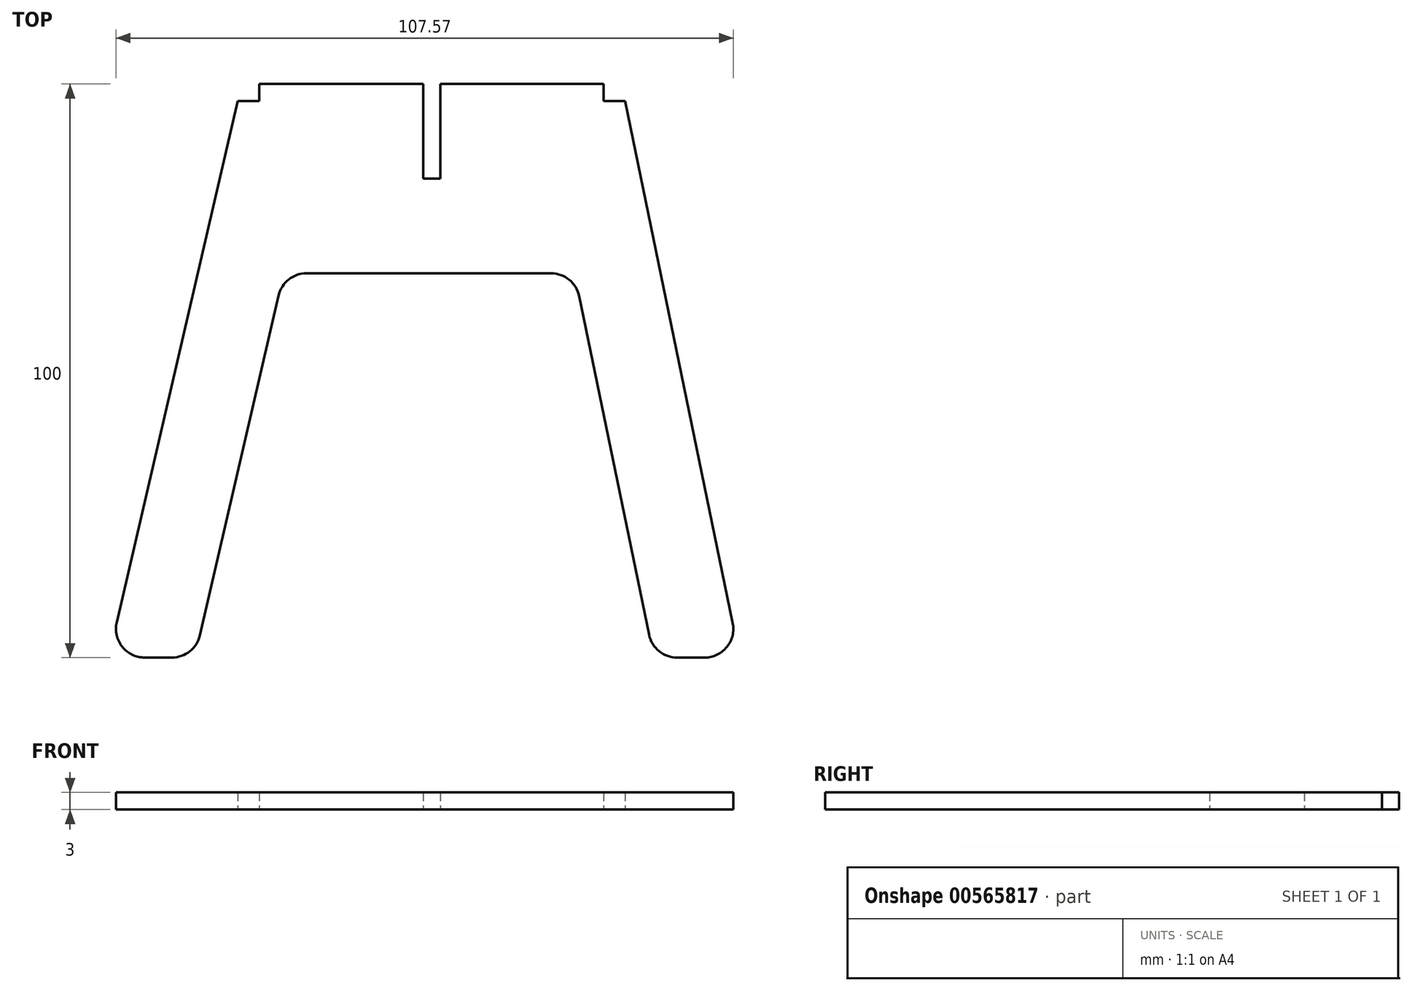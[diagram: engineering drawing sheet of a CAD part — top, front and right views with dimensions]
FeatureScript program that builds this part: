
annotation { "Feature Type Name" : "Feature", "Feature Type Description" : "" }
export const myFeature = defineFeature(function(context is Context, id is Id, definition is map)
    precondition{}
    {
        {
            var Q0;
            Q0=qCreatedBy(makeId("Top.planeOp"),FACE);
            var sketch = newSketch(context, id + "F0", { "sketchPlane" : qUnion([Q0])});
            skLineSegment(sketch, "E0.bottom", {"start": v(-30.08, 50.11) * mm, "end": v(-1.5, 50.11) * mm});
            skLineSegment(sketch, "E0.top", {"start": v(-50.03, -49.89) * mm, "end": v(-45.3, -49.89) * mm});
            skLineSegment(sketch, "E1", {"start": v(-33.84, 47.11) * mm, "end": v(-30.08, 47.11) * mm});
            skLineSegment(sketch, "E2", {"start": v(-30.08, 47.11) * mm, "end": v(-30.08, 50.11) * mm});
            skLineSegment(sketch, "E3", {"start": v(29.92, 47.11) * mm, "end": v(29.92, 50.11) * mm});
            skLineSegment(sketch, "E4", {"start": v(-21.82, 17.11) * mm, "end": v(20.79, 17.11) * mm});
            skLineSegment(sketch, "E5", {"start": v(33.67, 47.11) * mm, "end": v(52.44, -43.88) * mm});
            skLineSegment(sketch, "E6", {"start": v(-54.9, -43.76) * mm, "end": v(-33.84, 47.11) * mm});
            skLineSegment(sketch, "E7", {"start": v(-40.43, -46.02) * mm, "end": v(-26.7, 13.24) * mm});
            skLineSegment(sketch, "E8", {"start": v(25.68, 13.12) * mm, "end": v(37.85, -45.9) * mm});
            skLineSegment(sketch, "E9.trimOffspring", {"start": v(42.75, -49.89) * mm, "end": v(47.54, -49.89) * mm});
            skLineSegment(sketch, "E10.trimOffspring", {"start": v(29.92, 47.11) * mm, "end": v(33.67, 47.11) * mm});
            skPoint(sketch, "E11.visualSharp", {"position": v(-56.33, -49.89) * mm});
            skArc(sketch, "E11.filletArc", {"start": v(-54.9, -43.76) * mm, "mid": v(-53.95, -48) * mm, "end": v(-50.03, -49.89) * mm});
            skPoint(sketch, "E12.visualSharp", {"position": v(-41.33, -49.89) * mm});
            skArc(sketch, "E12.filletArc", {"start": v(-45.3, -49.89) * mm, "mid": v(-42.19, -48.8) * mm, "end": v(-40.43, -46.02) * mm});
            skPoint(sketch, "E13.visualSharp", {"position": v(38.67, -49.89) * mm});
            skArc(sketch, "E13.filletArc", {"start": v(37.85, -45.9) * mm, "mid": v(39.59, -48.77) * mm, "end": v(42.75, -49.89) * mm});
            skPoint(sketch, "E14.visualSharp", {"position": v(53.67, -49.89) * mm});
            skArc(sketch, "E14.filletArc", {"start": v(47.54, -49.89) * mm, "mid": v(51.41, -48.05) * mm, "end": v(52.44, -43.88) * mm});
            skPoint(sketch, "E15.visualSharp", {"position": v(-25.8, 17.11) * mm});
            skArc(sketch, "E15.filletArc", {"start": v(-21.82, 17.11) * mm, "mid": v(-24.93, 16.03) * mm, "end": v(-26.7, 13.24) * mm});
            skPoint(sketch, "E16.visualSharp", {"position": v(24.86, 17.11) * mm});
            skArc(sketch, "E16.filletArc", {"start": v(25.68, 13.12) * mm, "mid": v(23.94, 15.99) * mm, "end": v(20.79, 17.11) * mm});
            skLineSegment(sketch, "E17", {"start": v(0, 50.11) * mm, "end": v(0, 17.11) * mm, "construction": true});
            skLineSegment(sketch, "E18", {"start": v(1.5, 50.11) * mm, "end": v(1.5, 33.61) * mm});
            skPoint(sketch, "E18.endSnap0", {"position": v(0, 33.61) * mm});
            skLineSegment(sketch, "E19.MirrorCS", {"start": v(-1.5, 50.11) * mm, "end": v(-1.5, 33.61) * mm});
            skLineSegment(sketch, "E20", {"start": v(0, 33.61) * mm, "end": v(-1.5, 33.61) * mm});
            skLineSegment(sketch, "E21", {"start": v(0, 33.61) * mm, "end": v(1.5, 33.61) * mm});
            skLineSegment(sketch, "E22.trimOffspring", {"start": v(1.5, 50.11) * mm, "end": v(29.92, 50.11) * mm});
            skSolve(sketch);
        }
        {
            var Q0;
            Q0 = qSketchRegion(id + "F0", true);
            extrude(context, id + "F1", {"entities" : qUnion([Q0]), "depth" : 3 * mm, "offsetDistance" : 25 * mm});
        }
    });
